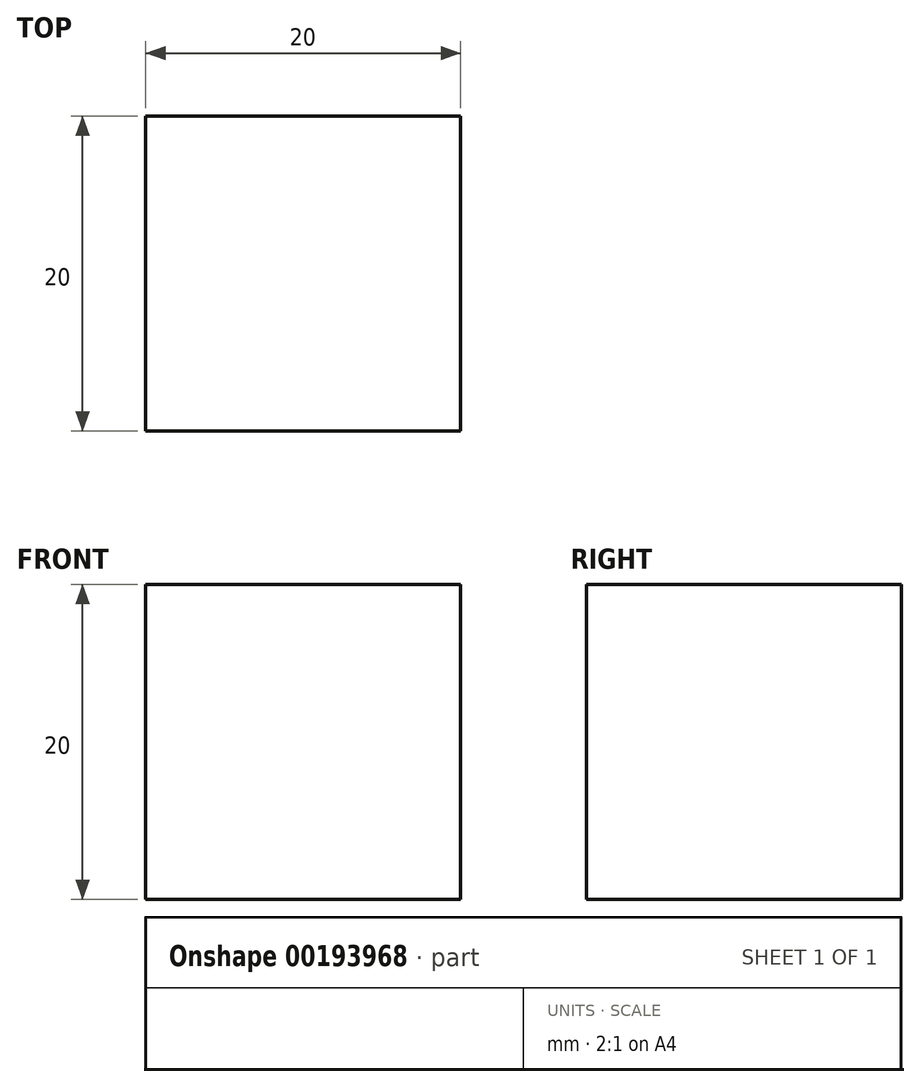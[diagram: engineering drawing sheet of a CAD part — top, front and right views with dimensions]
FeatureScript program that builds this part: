
annotation { "Feature Type Name" : "Feature", "Feature Type Description" : "" }
export const myFeature = defineFeature(function(context is Context, id is Id, definition is map)
    precondition{}
    {
        {
            var Q0;
            Q0=qCreatedBy(makeId("Front.planeOp"),FACE);
            var sketch = newSketch(context, id + "F0", { "sketchPlane" : qUnion([Q0])});
            skLineSegment(sketch, "E0.bottom", {"start": v(10, 10) * mm, "end": v(-10, 10) * mm});
            skLineSegment(sketch, "E0.top", {"start": v(10, -10) * mm, "end": v(-10, -10) * mm});
            skLineSegment(sketch, "E0.left", {"start": v(10, 10) * mm, "end": v(10, -10) * mm});
            skLineSegment(sketch, "E0.right", {"start": v(-10, 10) * mm, "end": v(-10, -10) * mm});
            skPoint(sketch, "E0.middle", {"position": v(0, 0) * mm});
            skSolve(sketch);
        }
        {
            var Q0;
            Q0=makeQuery(id+"F0.imprint","IMPRINT",FACE,{"disambiguationData":[TD([[makeQuery(id+"F0.imprint","IMPRINT",EDGE,{"derivedFrom":sQuery(id+"F0.wireOp",EDGE,"E0.bottom")}),1.0]])]});
            extrude(context, id + "F1", {"entities" : qUnion([Q0]), "depth" : 20 * mm});
        }
    });
